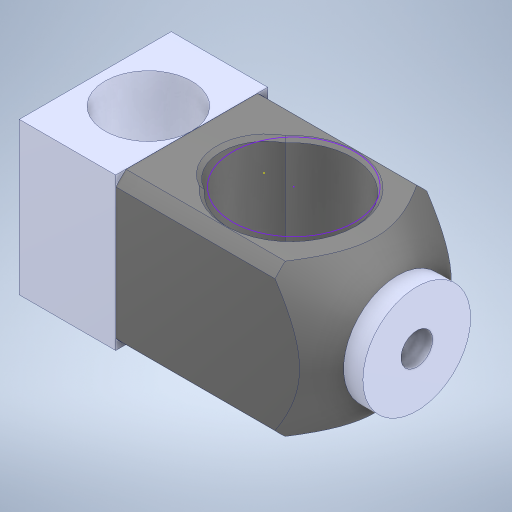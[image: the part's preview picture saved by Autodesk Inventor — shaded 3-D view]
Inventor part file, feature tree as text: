
AUTODESK INVENTOR PART (.ipt)
format: ipt  version: 2023 (Build 270158000, 158)  size: 340,992 bytes
history: mixed  units: in
note: dims shown in document units (in); Inventor stores cm internally (conversion verified against a paired STEP export)
features: sketch x8, extrude x7, other x1, imported_body x1
ambient origin geometry x8: Origin, YZ Plane, XZ Plane, XY Plane, X Axis, Y Axis, Z Axis, Center Point
bodies: Solid1 (imported_parasolid)
feature tree (17):
  other  "6669-001-1-solid1"
  extrude  "Extrusion1"  Depth=0.3937in
  sketch  "Sketch2"  dims[d8=0.3937in d9=0.0in d10=0.0in d11=0.0in]
  extrude  "Extrusion4"  TaperAngle=0.0deg  [1 undecoded]
  sketch  "Sketch5"  dims[d16=0.2165in d17=0.1969in]
  extrude  "Extrusion5"  Depth=0.3937in TaperAngle=0.0deg
  extrude  "Extrusion6"  Depth=0.1969in
  extrude  "Extrusion7"  Depth=0.3543in
  extrude  "Extrusion8"  Depth=0.0197in
  extrude  "Extrusion9"  Depth=0.0197in
  sketch  "Sketch1"  dims[d0=0.3937in d1=0.0in d7=0.1299in]
  sketch  "Sketch4"  dims[d12=0.0787in d13=0.0in d14=0.3937in d15=0.0in]
  sketch  "Sketch6"  dims[d18=0.1969in d19=0.0in d20=0.3543in]
  sketch  "Sketch7"  dims[d21=0.0in d22=0.0in d2=0.0197in]
  sketch  "Sketch8"  dims[d3=0.0344in d4=0.0197in]
  sketch  "Sketch9"  dims[d5=0.0344in]
  imported_body  NMx_Import_Brep_tag  [imported B-rep: ~19 faces, bbox_mm=[31.336, 15.765997, 15.763116]]
note: 1 required parameter value undecoded (feature->parameter linkage not recoverable at this tier; creation-order binding heuristic only, values carry confidence <= 0.55)
